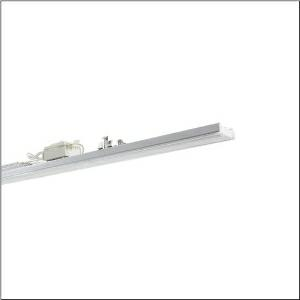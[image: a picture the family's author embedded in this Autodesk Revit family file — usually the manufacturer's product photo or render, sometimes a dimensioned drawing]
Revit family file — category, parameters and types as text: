
# Revit family: licross_r__11_recessed_ho_51tl12dn455md_fc93
name_source: partatom
category: Lighting Fixtures
units: mm (PartAtom-declared; Revit-internal decimal feet)

## family parameters
Cut with Voids When Loaded = No
Host = Face
Light Source = No
Part Type = Normal
Room Calculation Point = No
Round Connector Dimension = Use Diameter
Shared = No

## types (1)
- --- (1 x LED, 900 lm, 5.5 W, 4000K)
    Apparent Load = 6 VA
    CIE Flux Codes = 66 91 98 100 100
    Color Rendering = 80
    Color Temperature = 4000K
    Default Elevation = 1800 mm
    Description = Licross® 11 Recessed HO, luminaire insert, of sheet steel, coil coated, white, length: 1.500mm, width: 66mm, height: 67mm, LED rated luminous flux: 5.960lm, light colour: 840, control gear: DALI 2 (for two DALI lines), with plug, 6-pole, with phase selection, mains connection: 220..240V, AC/DC, 0/50..60Hz, rated input power: 31W, without changeover relay, for emergency light function, for central battery installations according to DIN EN 60598-2-22, halogen-free wiring, primary optical cover: cover, of PMMA, light emission: direct distribution, primary light characteristic: symmetric, protection rating (complete): IP40, insulation class (complete): insulation class I (protective earthing), certification: CE, ENEC, VDE, UKCA, protection symbol: D if used in an environment without relevant dust loads with corresponding accessories, impact resistance: IK06, permissible ambient temperature for indoor applications: -25..+45°C, standard: EN 60598-2-22, corresponds to IFS (International Featured Standards) requirements for safety and quality in the food industry, reducing of maximum allowable ambient temperature of 5°C with ceiling mounting, LABS conformity tested according to VDMA 24364:2018-05, packaging unit: 1 piece
    Height = 58 mm
    Lamp = 1 x LED
    Lamp Light Flux = 900 lm
    Lamp Power = 5.5 W
    Lamp count = 1
    Length = 1500 mm
    Luminous efficacy = 164 lm/W
    Manufacturer = Siteco
    ModVariant = No
    Model = 51TL12DN455MD
    Mounting Place = Ceiling
    Mounting Type = Pendant
    Number of Poles = 1
    OnlyDefault = Yes
    Power Factor = 1
    Product Name = Licross® 11 Recessed HO
    Product group = luminaire insert
    ProductGroupID = 902
    Protection Class = Protection class I
    Protection Degree = IP 40
    RLX_Detail_Level = 1
    RLX_Emergency_Light_Flux = 0 lm
    RLX_Emergency_Type = 0
    RLX_Emergency_Type_DB = No
    RlxData = <blob elided: 24701 chars, md5=1357829b>
    Socket = socket
    Standby Power = 0 W
    System Light Flux = 900 lm
    System Power = 6 W
    Type Comments = : DC mode (central or group accumulator) initial emergency light level
    Type Image = l_1296930.jpg
    URL = http://relux.com
    VarID = @adj_087258
    Voltage = 0 V
    Weight = 0.00 kg
    Width = 66 mm

## geometry (parser evidence)
native form markers: Blend x4, Sweep x13
no freeform markers — native parametric forms only
